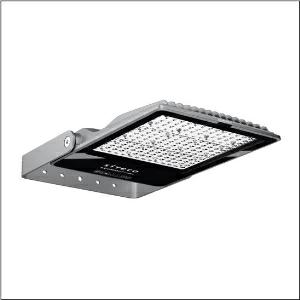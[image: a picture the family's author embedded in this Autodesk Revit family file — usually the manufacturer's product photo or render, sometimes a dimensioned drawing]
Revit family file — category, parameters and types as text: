
# Revit family: sicompact_31_midi___pl32_5xa7581d1k23_9d9b
name_source: partatom
category: Lighting Fixtures
units: mm (PartAtom-declared; Revit-internal decimal feet)

## family parameters
Cut with Voids When Loaded = No
Host = Face
Light Source = No
Part Type = Normal
Room Calculation Point = No
Round Connector Dimension = Use Diameter
Shared = No

## types (1)
- SiCompact 31 midi  PL32 (1 x LED, 27000 lm, 171 W, 3000K)
    Apparent Load = 171 VA
    CIE Flux Codes = 32 69 98 100 100
    Color Rendering = 70
    Color Temperature = 3000K
    Default Elevation = 1800 mm
    Description = SiCompact 31 midi, floodlight, primary light control with lens, of plastic, of toughened safety glass, transparent, light distribution: PL32, light emission: direct distribution, primary light characteristic: asymmetric, installation type: surface-mounted, LED, High Power LED, rated luminous flux: 27.000lm, luminous efficacy: 158lm/W, light colour: 730, colour temperature: 3000K, control gear: ON/OFF, with cable, 3x 1.5mm², mains connection: 220..240V, AC, 50/60Hz, connection cable pre-assembled, cable length: 2m, rated input power: 171W, of diecast aluminium, specular, metallic grey (RAL 9006), length: 560mm, width: 330mm, height: 62mm, bracket, of sheet steel, coated, metallic grey (RAL 9006), ON/OFF, protection rating (complete): IP66, insulation class (complete): insulation class I (protective earthing), certification: CE, ENEC, impact resistance: IK08, permissible operating ambient temperature: -40..+45°C, packaging unit: 1 piece

Light Distribution: PL32
    Height = 62 mm  [stored 0.203412 ft]
    Lamp = 1 x LED
    Lamp Light Flux = 27000 lm
    Lamp Power = 171 W
    Lamp count = 1
    Length = 560 mm
    Luminous efficacy = 158 lm/W
    Manufacturer = Siteco
    ModVariant = No
    Model = 5XA7581D1K23
    Mounting Place = Wall
    Mounting Type = Surface mounted
    Number of Poles = 1
    OnlyDefault = Yes
    Power Factor = 1
    Product Name = SiCompact 31 midi | PL32
    Product group = floodlight | wall mounted
    ProductGroupID = 2002
    Protection Class = Protection class I
    Protection Degree = IP 66
    RLX_Detail_Level = 1
    RLX_Emergency_Light_Flux = 0 lm
    RLX_Emergency_Type = 0
    RLX_Emergency_Type_DB = No
    RlxData = <blob elided: 98369 chars, md5=5cac8427>
    Socket = socket
    Standby Power = 0 W
    System Light Flux = 27000 lm
    System Power = 171 W
    Type Comments = Product without accessories
    Type Image = l_1006415.jpg
    URL = http://relux.com
    VarID = ---
    Voltage = 0 V
    Weight = 0.00 kg
    Width = 333 mm

note: [stored X ft] marks values corroborated as IEEE doubles in the binary element streams (Revit-internal decimal feet)

## geometry (parser evidence)
native form markers: Blend x4, Sweep x14
no freeform markers — native parametric forms only
